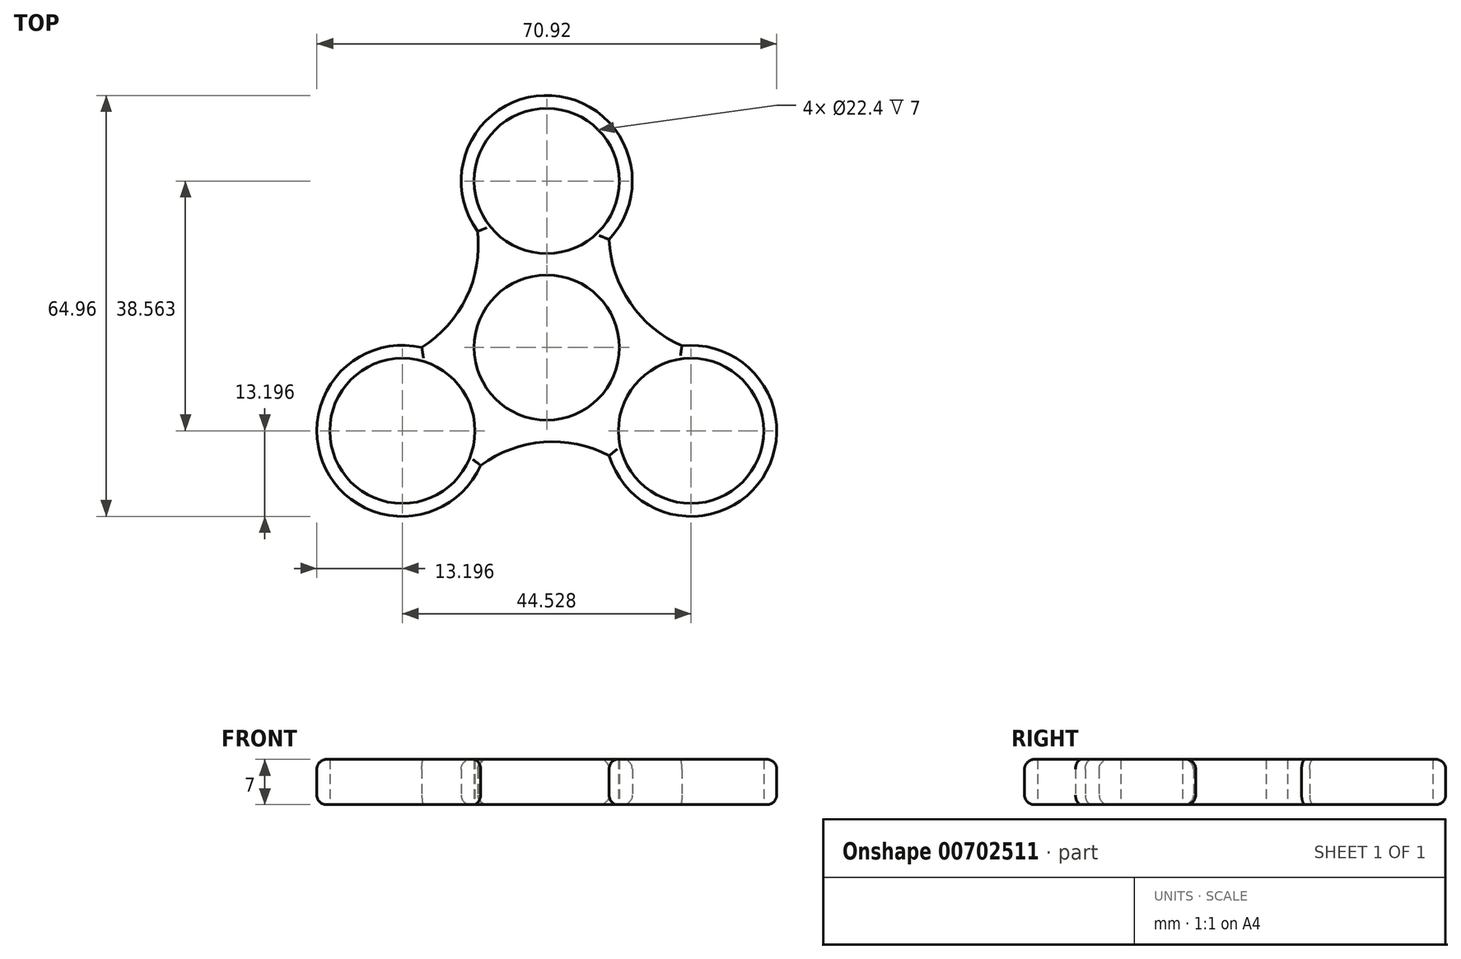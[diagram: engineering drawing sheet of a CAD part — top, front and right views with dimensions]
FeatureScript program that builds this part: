
annotation { "Feature Type Name" : "Feature", "Feature Type Description" : "" }
export const myFeature = defineFeature(function(context is Context, id is Id, definition is map)
    precondition{}
    {
        {
            var Q0;
            Q0=qCreatedBy(makeId("Top.planeOp"),FACE);
            var sketch = newSketch(context, id + "F0", { "sketchPlane" : qUnion([Q0])});
            skCircle(sketch, "E0", {"center": v(0, 0) * mm, "radius": 11.2 * mm});
            skCircle(sketch, "E1", {"center": v(0, 25.7) * mm, "radius": 11.2 * mm});
            skArc(sketch, "E2", {"start": v(9.63, 16.68) * mm, "mid": v(0.8, 38.88) * mm, "end": v(-10.66, 17.92) * mm});
            skCircle(sketch, "E3.1.0", {"center": v(-22.26, -12.85) * mm, "radius": 11.2 * mm});
            skArc(sketch, "E3.1.1", {"start": v(-19.26, 0) * mm, "mid": v(-34.08, -18.74) * mm, "end": v(-10.2, -18.2) * mm});
            skCircle(sketch, "E3.2.0", {"center": v(22.26, -12.85) * mm, "radius": 11.2 * mm});
            skArc(sketch, "E3.2.1", {"start": v(9.63, -16.68) * mm, "mid": v(33.27, -20.14) * mm, "end": v(20.85, 0.27) * mm});
            skArc(sketch, "E4", {"start": v(-19.26, 0) * mm, "mid": v(-12.4, 7.73) * mm, "end": v(-10.66, 17.92) * mm});
            skArc(sketch, "E5.1.0", {"start": v(9.63, -16.68) * mm, "mid": v(-0.5, -14.6) * mm, "end": v(-10.2, -18.2) * mm});
            skArc(sketch, "E5.2.0", {"start": v(9.63, 16.68) * mm, "mid": v(12.89, 6.87) * mm, "end": v(20.85, 0.27) * mm});
            skSolve(sketch);
        }
        {
            var Q0;
            Q0=makeQuery(id+"F0.imprint","IMPRINT",FACE,{"disambiguationData":[TD([[makeQuery(id+"F0.imprint","IMPRINT",EDGE,{"derivedFrom":sQuery(id+"F0.wireOp",EDGE,"E0")}),-1.0]])]});
            extrude(context, id + "F1", {"entities" : qUnion([Q0]), "depth" : 7 * mm, "offsetDistance" : 25 * mm});
        }
        {
            var Q0;
            Q0=makeQuery(id+"F1.opExtrude","CAP_EDGE",EDGE,{"disambiguationData":[OSD([sQuery(id+"F0.wireOp",EDGE,"E2")])],"isStart":false});
            var Q1;
            Q1=makeQuery(id+"F1.opExtrude","CAP_EDGE",EDGE,{"disambiguationData":[OSD([sQuery(id+"F0.wireOp",EDGE,"E5.2.0")])],"isStart":false});
            var Q2;
            Q2=makeQuery(id+"F1.opExtrude","CAP_EDGE",EDGE,{"disambiguationData":[OSD([sQuery(id+"F0.wireOp",EDGE,"E3.2.1")])],"isStart":false});
            var Q3;
            Q3=makeQuery(id+"F1.opExtrude","CAP_EDGE",EDGE,{"disambiguationData":[OSD([sQuery(id+"F0.wireOp",EDGE,"E5.1.0")])],"isStart":false});
            var Q4;
            Q4=makeQuery(id+"F1.opExtrude","CAP_EDGE",EDGE,{"disambiguationData":[OSD([sQuery(id+"F0.wireOp",EDGE,"E3.1.1")])],"isStart":false});
            var Q5;
            Q5=makeQuery(id+"F1.opExtrude","CAP_EDGE",EDGE,{"disambiguationData":[OSD([sQuery(id+"F0.wireOp",EDGE,"E4")])],"isStart":false});
            var Q6;
            Q6=makeQuery(id+"F1.opExtrude","CAP_EDGE",EDGE,{"disambiguationData":[OSD([sQuery(id+"F0.wireOp",EDGE,"E2")])],"isStart":true});
            var Q7;
            Q7=makeQuery(id+"F1.opExtrude","CAP_EDGE",EDGE,{"disambiguationData":[OSD([sQuery(id+"F0.wireOp",EDGE,"E5.2.0")])],"isStart":true});
            var Q8;
            Q8=makeQuery(id+"F1.opExtrude","CAP_EDGE",EDGE,{"disambiguationData":[OSD([sQuery(id+"F0.wireOp",EDGE,"E3.2.1")])],"isStart":true});
            var Q9;
            Q9=makeQuery(id+"F1.opExtrude","CAP_EDGE",EDGE,{"disambiguationData":[OSD([sQuery(id+"F0.wireOp",EDGE,"E5.1.0")])],"isStart":true});
            var Q10;
            Q10=makeQuery(id+"F1.opExtrude","CAP_EDGE",EDGE,{"disambiguationData":[OSD([sQuery(id+"F0.wireOp",EDGE,"E3.1.1")])],"isStart":true});
            var Q11;
            Q11=makeQuery(id+"F1.opExtrude","CAP_EDGE",EDGE,{"disambiguationData":[OSD([sQuery(id+"F0.wireOp",EDGE,"E4")])],"isStart":true});
            fillet(context, id + "F2", {"entities" : qUnion([Q0, Q1, Q2, Q3, Q4, Q5, Q6, Q7, Q8, Q9, Q10, Q11]), "radius" : 1.5 * mm, "tangentPropagation" : true, "allowEdgeOverflow" : false});
        }
    });
